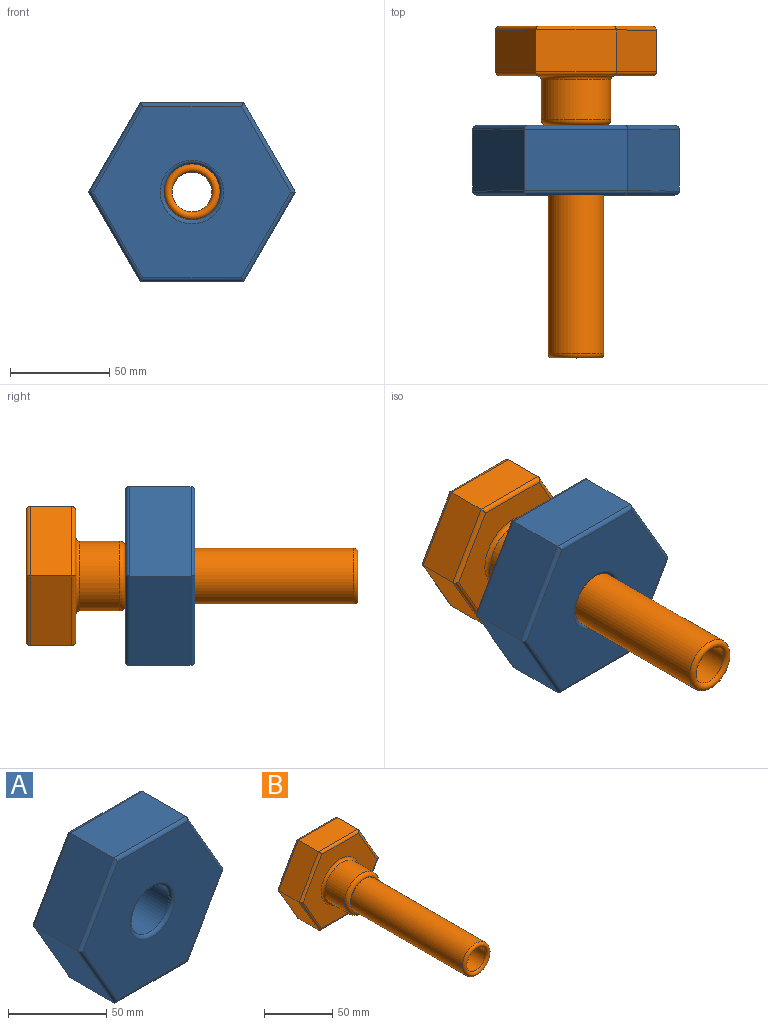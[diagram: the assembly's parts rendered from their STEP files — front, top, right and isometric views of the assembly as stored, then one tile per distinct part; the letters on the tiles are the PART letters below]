
ASSEMBLY  parts=2 mates=1
PART A: 23 faces, bbox 103.9x35x90 mm
  f0: plane 45x31mm, normal (-0.87,0,-0.5), area 1610.8mm2, adj f1,f5,f13,f19
  f1: plane 51.96x31mm, normal (0,0,-1), area 1610.8mm2, adj f0,f2,f11,f17
  f2: plane 45x31mm, normal (0.87,0,-0.5), area 1610.8mm2, adj f1,f3,f12,f18
  f3: plane 45x31mm, normal (0.87,0,0.5), area 1610.8mm2, adj f2,f4,f14,f20
  f4: plane 51.96x31mm, normal (0,0,1), area 1610.8mm2, adj f3,f5,f16,f22
  f5: plane 45x31mm, normal (-0.87,0,0.5), area 1610.8mm2, adj f0,f4,f15,f21
  f6: plane 99.3x86mm, normal (0,-1,0), area 5600.9mm2, adj f9,f17,f18,f19,f20,f21,f22
  f7: plane 99.3x86mm, normal (0,1,0), area 5600.9mm2, adj f10,f11,f12,f13,f14,f15,f16
  f8: cylinder r=14mm len=31mm, axis (0,-1,0), area 2726.9mm2, adj f9,f10
  f9: torus R=16mm, axis (0,-1,0), area 290.7mm2, adj f6,f8
  f10: torus R=16mm, axis (0,-1,0), area 290.7mm2, adj f7,f8
  f11: cylinder r=2mm len=51.96mm, axis (1,0,0), area 160.6mm2, adj f1,f7,f12,f13
  f12: cylinder r=2mm len=46mm, axis (0.5,0,0.87), area 160.6mm2, adj f2,f7,f11,f14
  f13: cylinder r=2mm len=46mm, axis (0.5,0,-0.87), area 160.6mm2, adj f0,f7,f11,f15
  f14: cylinder r=2mm len=46mm, axis (-0.5,0,0.87), area 160.6mm2, adj f3,f7,f12,f16
  f15: cylinder r=2mm len=46mm, axis (-0.5,0,-0.87), area 160.6mm2, adj f5,f7,f13,f16
  f16: cylinder r=2mm len=51.96mm, axis (-1,0,0), area 160.6mm2, adj f4,f7,f14,f15
  f17: cylinder r=2mm len=51.96mm, axis (-1,0,0), area 160.6mm2, adj f1,f6,f18,f19
  f18: cylinder r=2mm len=46mm, axis (-0.5,0,-0.87), area 160.6mm2, adj f2,f6,f17,f20
  f19: cylinder r=2mm len=46mm, axis (-0.5,0,0.87), area 160.6mm2, adj f0,f6,f17,f21
  f20: cylinder r=2mm len=46mm, axis (0.5,0,-0.87), area 160.6mm2, adj f3,f6,f18,f22
  f21: cylinder r=2mm len=46mm, axis (0.5,0,0.87), area 160.6mm2, adj f5,f6,f19,f22
  f22: cylinder r=2mm len=51.96mm, axis (1,0,0), area 160.6mm2, adj f4,f6,f20,f21
PART B: 28 faces, bbox 80.8x167x70 mm
  f0: plane 35x21mm, normal (0.87,0,0.5), area 848.7mm2, adj f1,f5,f15,f21
  f1: plane 40.41x21mm, normal (0,0,1), area 848.7mm2, adj f0,f2,f13,f19
  f2: plane 35x21mm, normal (-0.87,0,0.5), area 848.7mm2, adj f1,f3,f14,f20
  f3: plane 35x21mm, normal (-0.87,0,-0.5), area 848.7mm2, adj f2,f4,f16,f22
  f4: plane 40.41x21mm, normal (0,0,-1), area 848.7mm2, adj f3,f5,f18,f24
  f5: plane 35x21mm, normal (0.87,0,-0.5), area 848.7mm2, adj f0,f4,f17,f23
  f6: plane 76.21x66mm, normal (0,-1,0), area 2577.8mm2, adj f12,f19,f20,f21,f22,f23,f24
  f7: plane 76.21x66mm, normal (0,1,0), area 3065.5mm2, adj f13,f14,f15,f16,f17,f18,f26
  f8: cylinder r=17.5mm len=35mm, axis (0,1,0), area 2199.1mm2, adj f10,f12
  f9: plane 29x29mm, normal (0,-1,0), area 44.8mm2, adj f10,f11
  f10: torus R=14.5mm, axis (0,-1,0), area 485.9mm2, adj f8,f9
  f11: cylinder r=14mm len=115mm, axis (0,1,0), area 10115.9mm2, adj f9,f27
  f12: torus R=19.5mm, axis (0,-1,0), area 359.8mm2, adj f6,f8
  f13: cylinder r=2mm len=40.41mm, axis (-1,0,0), area 124.3mm2, adj f1,f7,f14,f15
  f14: cylinder r=2mm len=36mm, axis (-0.5,0,-0.87), area 124.3mm2, adj f2,f7,f13,f16
  f15: cylinder r=2mm len=36mm, axis (-0.5,0,0.87), area 124.3mm2, adj f0,f7,f13,f17
  f16: cylinder r=2mm len=36mm, axis (0.5,0,-0.87), area 124.3mm2, adj f3,f7,f14,f18
  f17: cylinder r=2mm len=36mm, axis (0.5,0,0.87), area 124.3mm2, adj f5,f7,f15,f18
  f18: cylinder r=2mm len=40.41mm, axis (1,0,0), area 124.3mm2, adj f4,f7,f16,f17
  f19: cylinder r=2mm len=40.41mm, axis (1,0,0), area 124.3mm2, adj f1,f6,f20,f21
  f20: cylinder r=2mm len=36mm, axis (0.5,0,0.87), area 124.3mm2, adj f2,f6,f19,f22
  f21: cylinder r=2mm len=36mm, axis (0.5,0,-0.87), area 124.3mm2, adj f0,f6,f19,f23
  f22: cylinder r=2mm len=36mm, axis (-0.5,0,0.87), area 124.3mm2, adj f3,f6,f20,f24
  f23: cylinder r=2mm len=36mm, axis (-0.5,0,-0.87), area 124.3mm2, adj f5,f6,f21,f24
  f24: cylinder r=2mm len=40.41mm, axis (-1,0,0), area 124.3mm2, adj f4,f6,f22,f23
  f25: cylinder r=10mm len=160mm, axis (0,1,0), area 10053.1mm2, adj f26,f27
  f26: torus R=15mm, axis (0,-1,0), area 583.1mm2, adj f7,f25
  f27: torus R=12mm, axis (0,-1,0), area 473.7mm2, adj f11,f25
PLACE A t=(-43.15,53.09,-75.97)mm
PLACE B t=(-43.15,103.09,-75.97)mm
MATE revolute B.f8 <-> A.f8  axis (0,-1,0) through (-43.15,53.09,-75.97)mm
